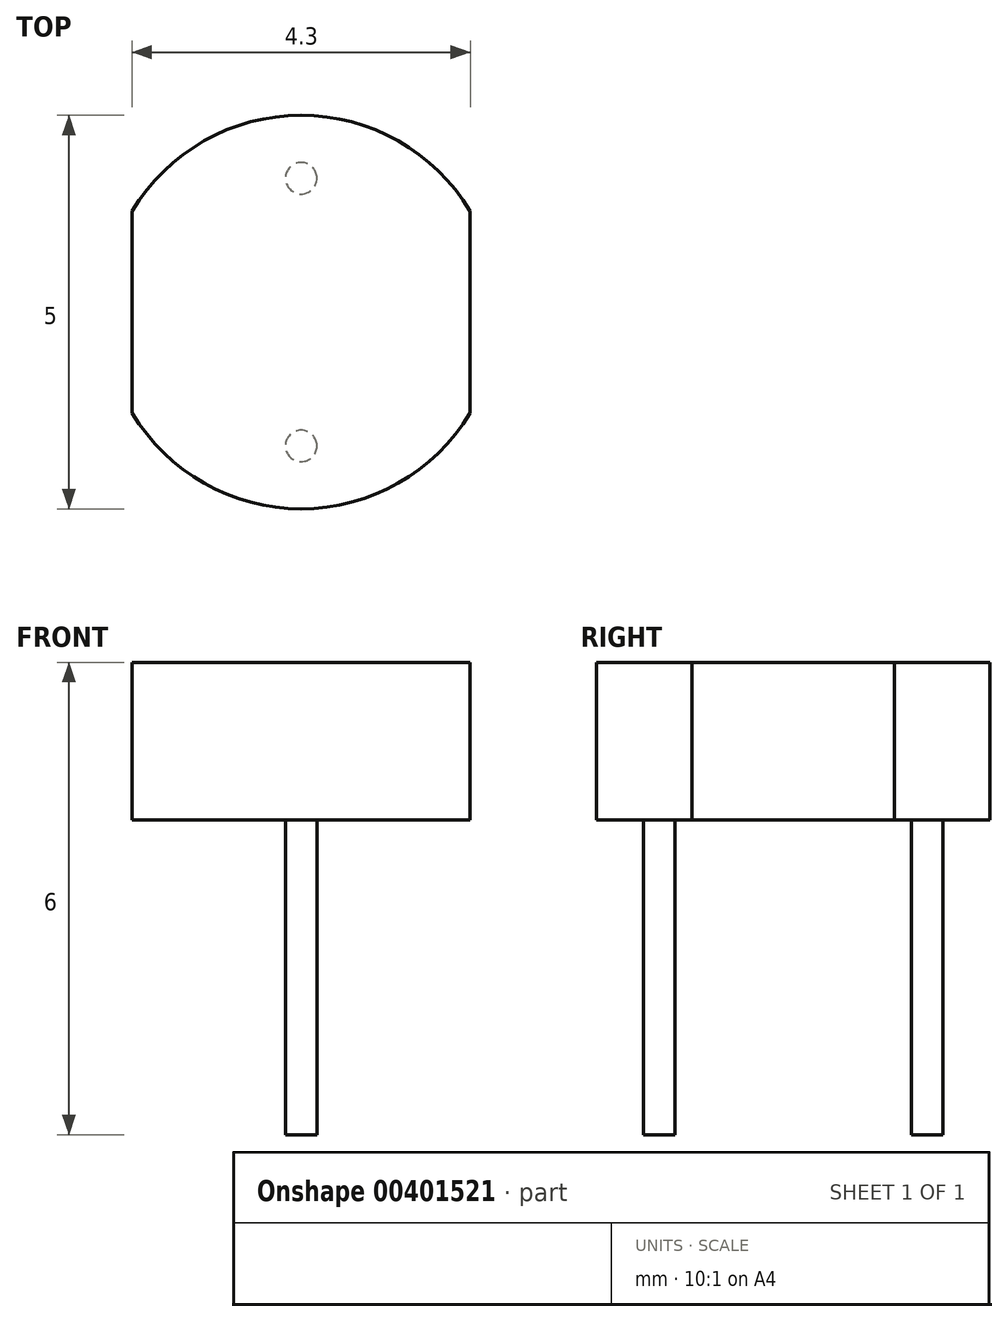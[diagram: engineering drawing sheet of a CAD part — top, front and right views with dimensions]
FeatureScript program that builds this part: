
annotation { "Feature Type Name" : "Feature", "Feature Type Description" : "" }
export const myFeature = defineFeature(function(context is Context, id is Id, definition is map)
    precondition{}
    {
        {
            var Q0;
            Q0=qCreatedBy(makeId("Top.planeOp"),FACE);
            var sketch = newSketch(context, id + "F0", { "sketchPlane" : qUnion([Q0])});
            skArc(sketch, "E0", {"start": v(-2.14, -1.28) * mm, "mid": v(0, -2.5) * mm, "end": v(2.15, -1.28) * mm});
            skLineSegment(sketch, "E1.top", {"start": v(2.15, -3.3) * mm, "end": v(-2.15, -3.3) * mm, "construction": true});
            skLineSegment(sketch, "E1.left", {"start": v(2.15, 1.28) * mm, "end": v(2.15, -1.28) * mm});
            skLineSegment(sketch, "E1.right", {"start": v(-2.14, 1.28) * mm, "end": v(-2.14, -1.28) * mm});
            skArc(sketch, "E2.trimOffspring", {"start": v(2.15, 1.28) * mm, "mid": v(0, 2.5) * mm, "end": v(-2.14, 1.28) * mm});
            skSolve(sketch);
        }
        {
            var Q0;
            Q0=qSketchRegion(id+"F0",true);
            extrude(context, id + "F1", {"entities" : qUnion([Q0]), "depth" : 2 * mm});
        }
        {
            var Q0;
            Q0=makeQuery(id+"F1.opExtrude","CAP_FACE",FACE,{"disambiguationData":[OSD([sQuery(id+"F0.wireOp",EDGE,"E0"),sQuery(id+"F0.wireOp",EDGE,"E1.left"),sQuery(id+"F0.wireOp",EDGE,"E1.right"),sQuery(id+"F0.wireOp",EDGE,"E2.trimOffspring")])],"isStart":true});
            var sketch = newSketch(context, id + "F2", { "sketchPlane" : qUnion([Q0])});
            skLineSegment(sketch, "E3", {"start": v(0, 0) * mm, "end": v(-4.1, 0) * mm, "construction": true});
            skLineSegment(sketch, "E4", {"start": v(0, -1.7) * mm, "end": v(-4.1, -1.7) * mm, "construction": true});
            skCircle(sketch, "E5", {"center": v(0, -1.7) * mm, "radius": 0.2 * mm});
            skCircle(sketch, "E6.MirrorC", {"center": v(0, 1.7) * mm, "radius": 0.2 * mm});
            skSolve(sketch);
        }
        {
            var Q0;
            Q0=qCreatedBy(makeId("Front.planeOp"),FACE);
            var sketch = newSketch(context, id + "F3", { "sketchPlane" : qUnion([Q0])});
            skLineSegment(sketch, "E7", {"start": v(0, 0) * mm, "end": v(0, -4) * mm});
            skSolve(sketch);
        }
        {
            var Q0;
            Q0=qSketchRegion(id+"F2",true);
            var Q1;
            Q1=qConstructionFilter(qBodyType(qCreatedBy(id+"F3",EDGE),BodyType.WIRE),ConstructionObject.NO);
            sweep(context, id + "F4", {"operationType" : NewBodyOperationType.ADD, "profiles" : qUnion([Q0]), "path" : qUnion([Q1])});
        }
    });
